# Revit family: HOTELLERIE MULTIPLE HOOK CHROME
name_source: partatom
category: Generic Models
units: mm (PartAtom-declared; Revit-internal decimal feet)

## family parameters
Can host rebar = No
Cut with Voids When Loaded = No
Host = Face
Part Type = Normal
Room Calculation Point = No
Round Connector Dimension = Use Diameter
Shared = No

## types (1)
- HOTELLERIE MULTIPLE HOOK CHROME
    Article Number = LG21281300000
    BIMobject Category = Furniture
    BIMobject QR code url = http://gedy-fi.bimobject.com
    Default Elevation = 1000 mm  [stored 3.28084 ft]
    Depth (mm) = 33 mm  [stored 0.108268 ft]
    Design country = Italy
    Edition number = 1
    IFC Classification = Furnishing Element
    Length (mm) = 195 mm  [stored 0.639764 ft]
    Manufacturer = Gedy-FI
    Manufacturer URL = http://www.laattapiste.fi
    Manufacturer country = Italy
    Material main = Chrome
    Model = HOTELLERIE MULTIPLE HOOK CHROME
    NBS Reference = 35-75-18
    NBS Reference Description = Clothes Hooks
    Name of the object = HOTELLERIE MULTIPLE HOOK CHROME
    Product SKU = LG21281300000
    Product data url = http://www.gedy.com
    Product family = Gedy
    Product group = Hotell
    Thickness (mm) = 11 mm  [stored 0.0360892 ft]
    UNSPC Category = Furniture and Furnishings
    UNSPC code = 56
    URL = http://gedy-fi.bimobject.com
    Uniclass 1.4 Code = L824
    Uniclass 1.4 Description = Bathroom, toilet furniture...
    Uniclass 2.0 Code = PR-35-75-18
    Uniclass 2.0 Description = Clothes Hooks
    Width (mm) = 40 mm  [stored 0.131234 ft]

note: [stored X ft] marks values corroborated as IEEE doubles in the binary element streams (Revit-internal decimal feet)

## geometry (parser evidence)
native form markers: Sweep x3
no freeform markers — native parametric forms only
